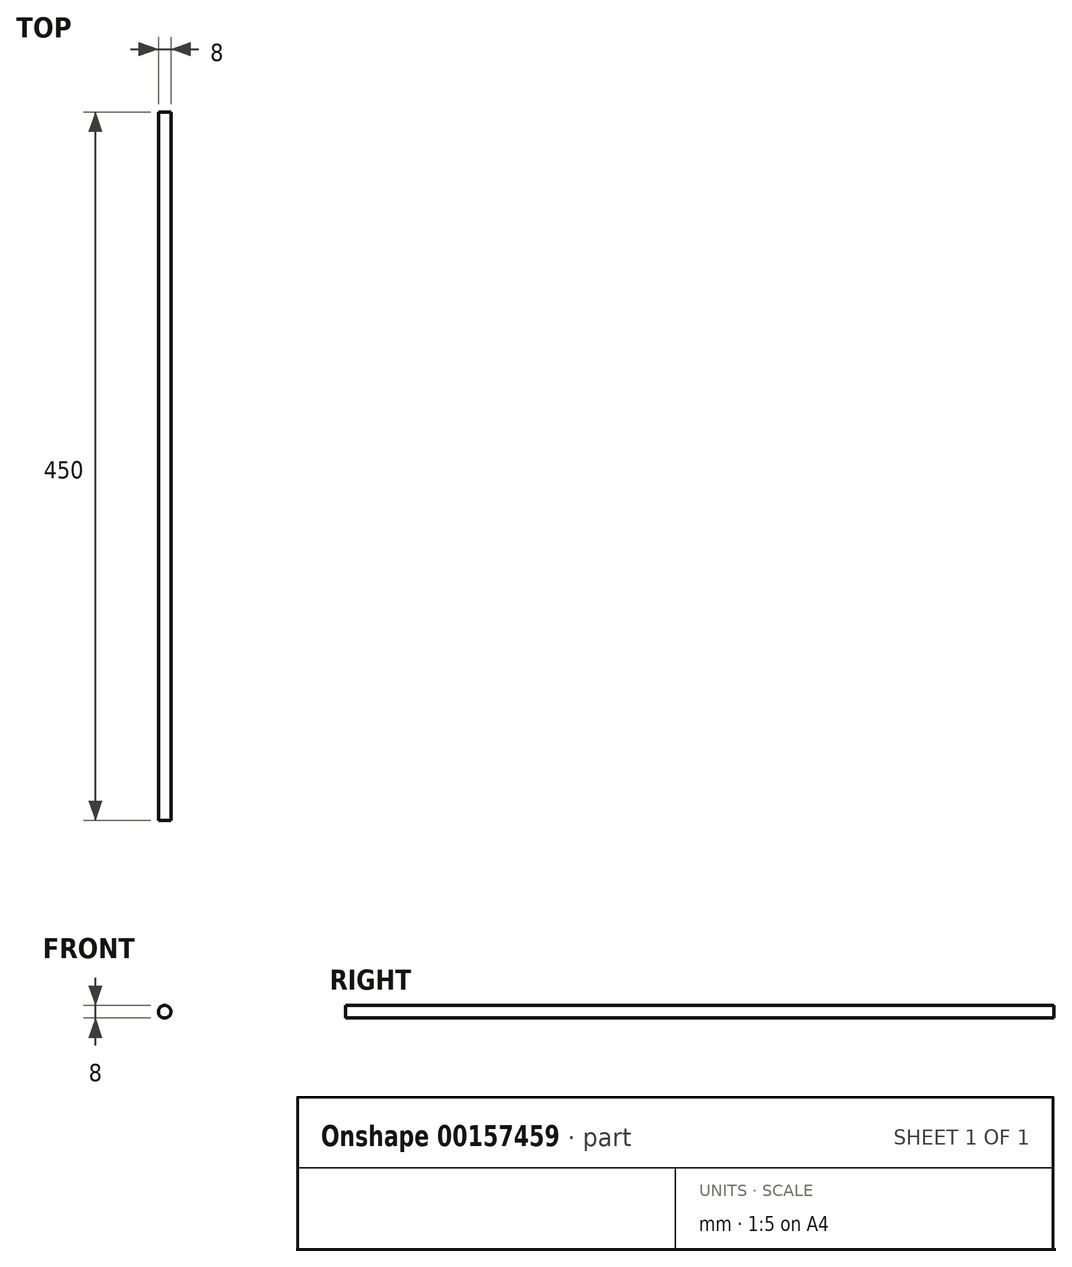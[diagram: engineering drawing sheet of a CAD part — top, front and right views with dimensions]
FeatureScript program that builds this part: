
annotation { "Feature Type Name" : "Feature", "Feature Type Description" : "" }
export const myFeature = defineFeature(function(context is Context, id is Id, definition is map)
    precondition{}
    {
        {
            var Q0;
            Q0=qCreatedBy(makeId("Front.planeOp"),FACE);
            var sketch = newSketch(context, id + "F0", { "sketchPlane" : qUnion([Q0])});
            skCircle(sketch, "E0", {"center": v(0, 0) * mm, "radius": 4 * mm});
            skSolve(sketch);
        }
        {
            var Q0;
            Q0=makeQuery(id+"F0.imprint","IMPRINT",FACE,{"disambiguationData":[TD([[makeQuery(id+"F0.imprint","IMPRINT",EDGE,{"derivedFrom":sQuery(id+"F0.wireOp",EDGE,"E0")}),1.0]])]});
            extrude(context, id + "F1", {"entities" : qUnion([Q0]), "depth" : 450 * mm});
        }
    });
